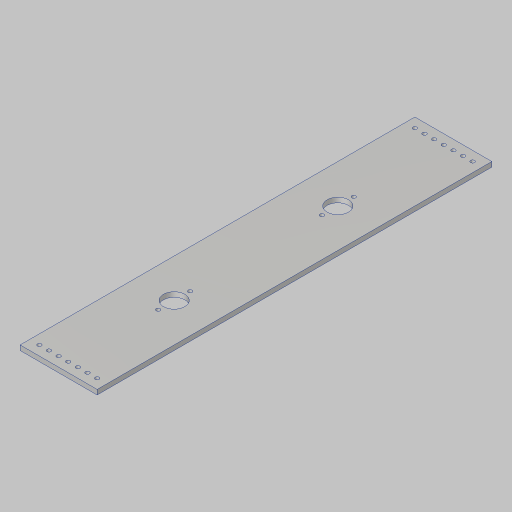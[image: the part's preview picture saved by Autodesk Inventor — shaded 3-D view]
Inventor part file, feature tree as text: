
AUTODESK INVENTOR PART (.ipt)
format: ipt  version: 2023.5 (Build 275446000, 446)  size: 140,288 bytes
history: native  units: in
note: dims shown in document units (in); Inventor stores cm internally (conversion verified against a paired STEP export)
features: sketch x4, extrude x2, hole x2, projected_geometry x1
ambient origin geometry x8: Origin, YZ Plane, XZ Plane, XY Plane, X Axis, Y Axis, Z Axis, Center Point
bodies: Solid1 (feature_tree)
feature tree (9):
  extrude  "Extrusion1"  Depth=20.5in
  extrude  "Extrusion2"  Depth=0.25in
  hole  "Hole1"  [1 undecoded]
  hole  "Hole2"  [1 undecoded]
  sketch  "Sketch1"  dims[d0=4.0in d1=20.5in]
  sketch  "Sketch2"  dims[d2=0.25in d3=0.0in d5=1.11in]
  sketch  "Sketch3"  dims[d7=5.0in d8=5.0in]
  sketch  "Sketch4"  dims[d9=3.5in d10=4.5in d12=6.0039in d13=0.25in d14=0.0in d15=0.5in d16=0.5in d17=2.7559in d19=0.5in d20=0.3937in d22=1.0in d24=0.201in d25=0.75in d26=0.385in d27=0.25in d28=0.5635in d29=1.0in d30=0.8108in d31=1.655in d32=1.655in d33=0.201in d34=0.75in d35=0.375in d36=0.25in d37=0.5635in d38=1.0in d39=0.8108in]
  projected_geometry  "Project Cut Edges1"
note: 2 required parameter values undecoded (feature->parameter linkage not recoverable at this tier; creation-order binding heuristic only, values carry confidence <= 0.55)
